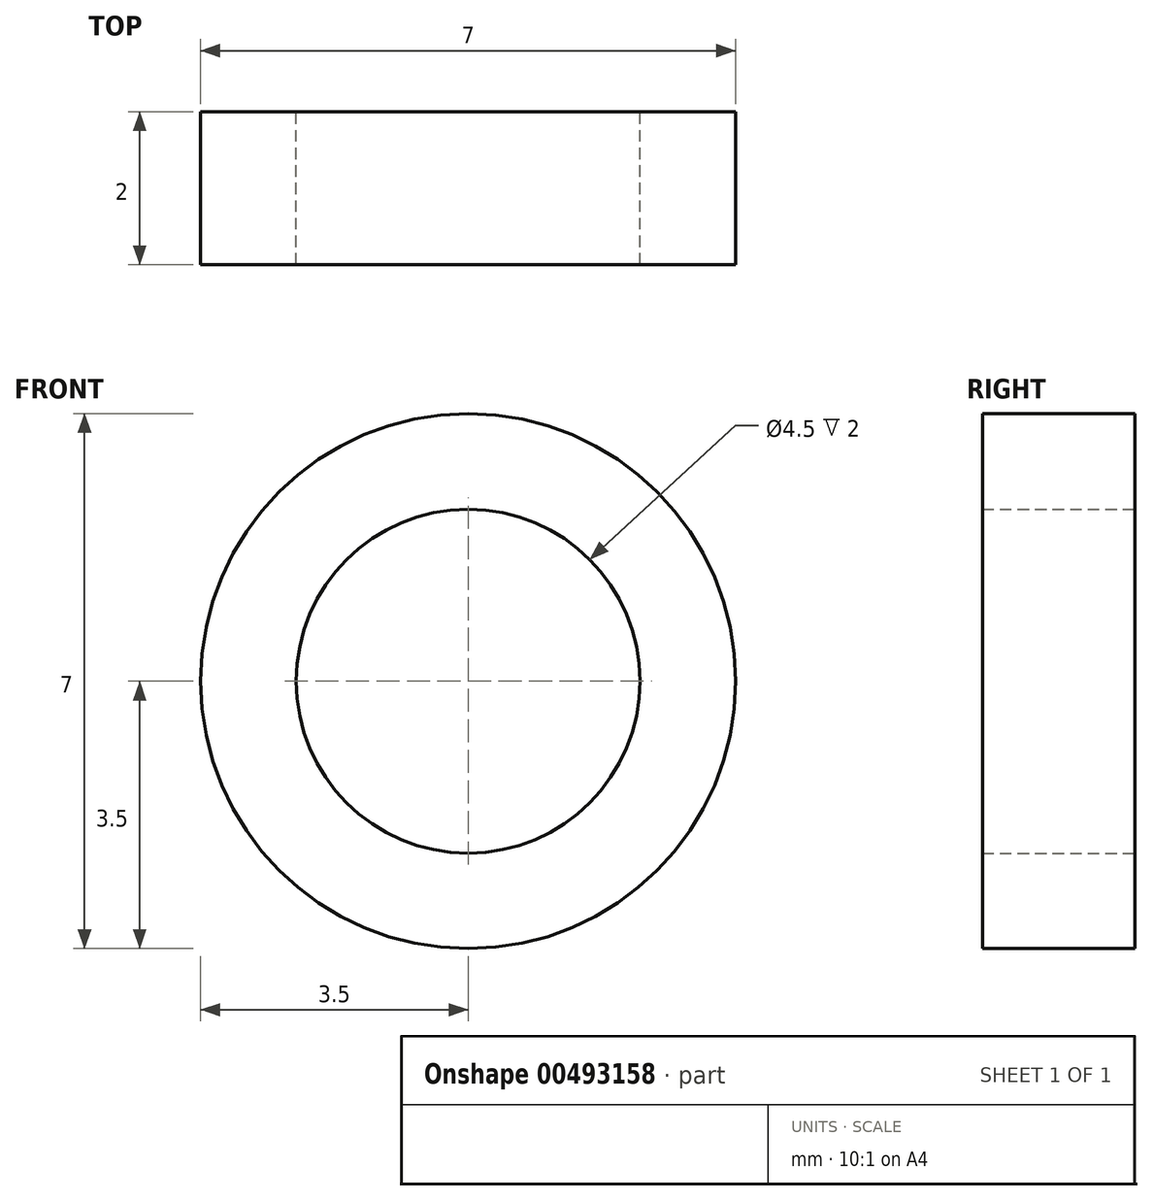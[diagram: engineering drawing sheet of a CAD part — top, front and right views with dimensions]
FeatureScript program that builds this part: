
annotation { "Feature Type Name" : "Feature", "Feature Type Description" : "" }
export const myFeature = defineFeature(function(context is Context, id is Id, definition is map)
    precondition{}
    {
        {
            var Q0;
            Q0=qCreatedBy(makeId("Front.planeOp"),FACE);
            var sketch = newSketch(context, id + "F0", { "sketchPlane" : qUnion([Q0])});
            skCircle(sketch, "E0", {"center": v(0, 0) * mm, "radius": 2.25 * mm});
            skCircle(sketch, "E1", {"center": v(0, 0) * mm, "radius": 3.5 * mm});
            skSolve(sketch);
        }
        {
            var Q0;
            Q0 = qSketchRegion(id + "F0", true);
            extrude(context, id + "F1", {"entities" : qUnion([Q0]), "depth" : 2 * mm});
        }
    });
